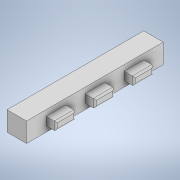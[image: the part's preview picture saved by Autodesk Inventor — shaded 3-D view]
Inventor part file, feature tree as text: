
AUTODESK INVENTOR PART (.ipt)
format: ipt  version: 2020 (Build 240168000, 168)  size: 141,824 bytes
history: native  units: mm
features: extrude x2, sketch x2, fillet x1
ambient origin geometry x8: Origin, YZ Plane, XZ Plane, XY Plane, X Axis, Y Axis, Z Axis, Center Point
bodies: Solid1 (feature_tree)
feature tree (5):
  extrude  "Extrusion1"  Depth=42.0mm
  extrude  "Extrusion2"  TaperAngle=0.0deg  [1 undecoded]
  fillet  "Fillet1"  Radius=6.0mm
  sketch  "Sketch1"  dims[d0=6.0mm d1=42.0mm]
  sketch  "Sketch2"  dims[d2=6.0mm d3=0.0mm d4=6.0mm d5=2.5mm d6=6.0mm d7=30.0mm d9=12.0mm d10=10.0mm d12=10.0mm d14=3.0mm d15=0.0mm d16=0.5mm]
note: 1 required parameter value undecoded (feature->parameter linkage not recoverable at this tier; creation-order binding heuristic only, values carry confidence <= 0.55)
